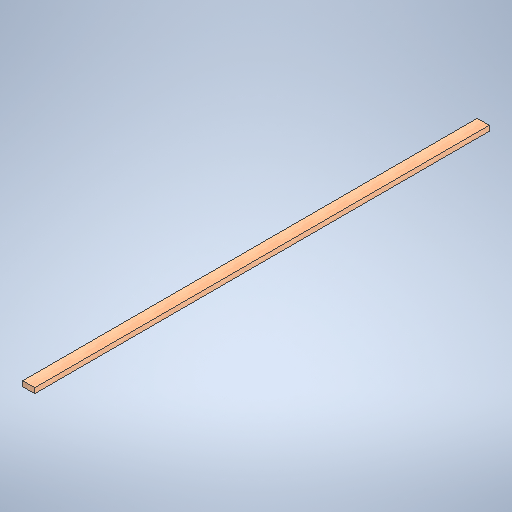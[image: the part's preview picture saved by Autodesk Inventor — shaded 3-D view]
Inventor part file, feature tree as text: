
AUTODESK INVENTOR PART (.ipt)
format: ipt  version: 2025 (Build 290162010, 162A)  size: 269,312 bytes
history: native  units: in
note: dims shown in document units (in); Inventor stores cm internally (conversion verified against a paired STEP export)
features: extrude x1, sketch x1
ambient origin geometry x8: Origin, YZ Plane, XZ Plane, XY Plane, X Axis, Y Axis, Z Axis, Center Point
bodies: Solid1 (feature_tree)
feature tree (2):
  extrude  "Extrusion1"  Depth=1.5in
  sketch  "Sketch1"  dims[d0=3.5in d1=1.5in d2=132.0in d3=0.0in]
